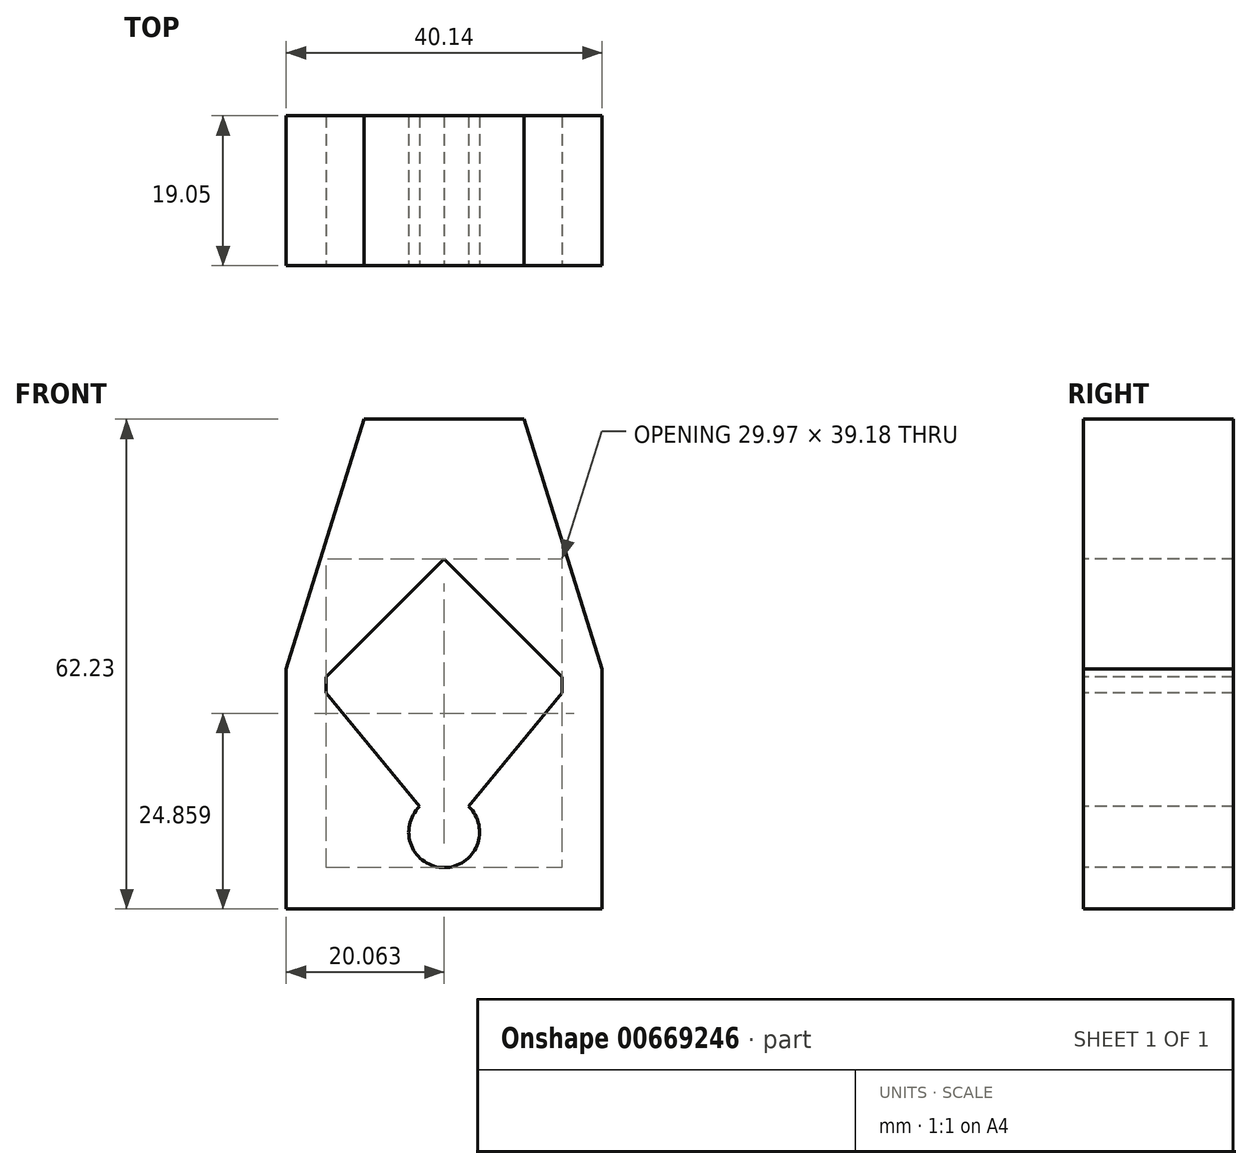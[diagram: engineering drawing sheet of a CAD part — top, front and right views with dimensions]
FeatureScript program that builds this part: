
annotation { "Feature Type Name" : "Feature", "Feature Type Description" : "" }
export const myFeature = defineFeature(function(context is Context, id is Id, definition is map)
    precondition{}
    {
        {
            var Q0;
            Q0=qCreatedBy(makeId("Top.planeOp"),FACE);
            var sketch = newSketch(context, id + "F0", { "sketchPlane" : qUnion([Q0])});
            skLineSegment(sketch, "E0.bottom", {"start": v(14.31, 31.85) * mm, "end": v(54.45, 31.85) * mm});
            skLineSegment(sketch, "E0.top", {"start": v(14.31, 12.8) * mm, "end": v(54.45, 12.8) * mm});
            skLineSegment(sketch, "E0.left", {"start": v(14.31, 31.85) * mm, "end": v(14.31, 12.8) * mm});
            skLineSegment(sketch, "E0.right", {"start": v(54.45, 31.85) * mm, "end": v(54.45, 12.8) * mm});
            skSolve(sketch);
        }
        {
            var Q0;
            Q0 = qSketchRegion(id + "F0", true);
            extrude(context, id + "F1", {"entities" : qUnion([Q0]), "depth" : 62.23 * mm, "offsetDistance" : 25.4 * mm});
        }
        {
            var Q0;
            Q0=makeQuery(id+"F1.opExtrude","SWEPT_FACE",FACE,{"disambiguationData":[OSD([sQuery(id+"F0.wireOp",EDGE,"E0.top")])]});
            var sketch = newSketch(context, id + "F2", { "sketchPlane" : qUnion([Q0])});
            skLineSegment(sketch, "E1", {"start": v(34.38, 62.23) * mm, "end": v(34.38, 0) * mm});
            skLineSegment(sketch, "E2", {"start": v(34.38, 44.45) * mm, "end": v(49.36, 29.47) * mm});
            skLineSegment(sketch, "E3", {"start": v(49.36, 29.47) * mm, "end": v(19.39, 29.47) * mm});
            skLineSegment(sketch, "E4", {"start": v(34.38, 44.45) * mm, "end": v(19.39, 29.47) * mm});
            skArc(sketch, "E5", {"start": v(31.26, 13.01) * mm, "mid": v(34.38, 5.27) * mm, "end": v(37.5, 13.01) * mm});
            skLineSegment(sketch, "E6", {"start": v(49.36, 29.47) * mm, "end": v(49.36, 27.44) * mm});
            skLineSegment(sketch, "E7", {"start": v(49.36, 27.44) * mm, "end": v(37.5, 13.01) * mm});
            skLineSegment(sketch, "E8", {"start": v(19.39, 29.47) * mm, "end": v(19.39, 27.44) * mm});
            skLineSegment(sketch, "E9", {"start": v(19.39, 27.44) * mm, "end": v(31.26, 13.01) * mm});
            skSolve(sketch);
        }
        {
            var Q0;
            Q0 = qSketchRegion(id + "F2", true);
            extrude(context, id + "F3", {"entities" : qUnion([Q0]), "operationType" : NewBodyOperationType.REMOVE, "oppositeDirection" : true, "depth" : 25.4 * mm, "offsetDistance" : 25.4 * mm});
        }
        {
            var Q0;
            Q0=makeQuery(id+"F1.opExtrude","SWEPT_FACE",FACE,{"disambiguationData":[OSD([sQuery(id+"F0.wireOp",EDGE,"E0.top")])]});
            var sketch = newSketch(context, id + "F4", { "sketchPlane" : qUnion([Q0])});
            skLineSegment(sketch, "E10", {"start": v(14.31, 30.48) * mm, "end": v(24.22, 62.23) * mm});
            skLineSegment(sketch, "E11", {"start": v(24.22, 62.23) * mm, "end": v(14.31, 62.23) * mm});
            skLineSegment(sketch, "E12", {"start": v(14.31, 62.23) * mm, "end": v(14.31, 30.48) * mm});
            skLineSegment(sketch, "E13", {"start": v(44.54, 62.23) * mm, "end": v(54.45, 30.48) * mm});
            skLineSegment(sketch, "E14", {"start": v(54.45, 30.48) * mm, "end": v(54.45, 62.23) * mm});
            skLineSegment(sketch, "E15", {"start": v(54.45, 62.23) * mm, "end": v(44.54, 62.23) * mm});
            skSolve(sketch);
        }
        {
            var Q0;
            Q0 = qSketchRegion(id + "F4", true);
            extrude(context, id + "F5", {"entities" : qUnion([Q0]), "operationType" : NewBodyOperationType.REMOVE, "oppositeDirection" : true, "depth" : 25.4 * mm, "offsetDistance" : 25.4 * mm});
        }
    });
